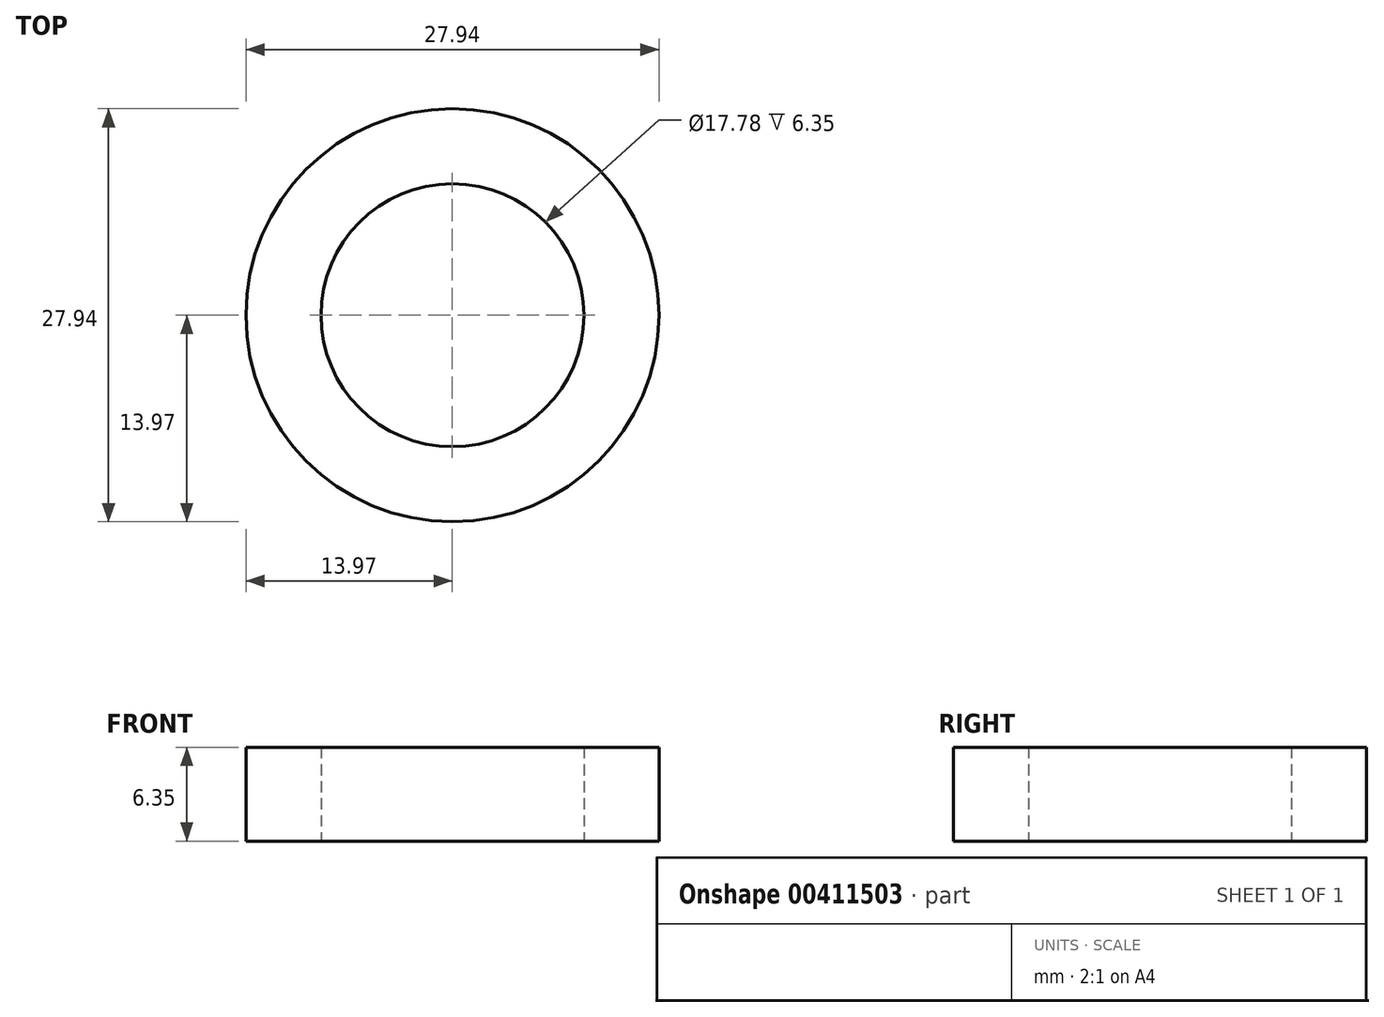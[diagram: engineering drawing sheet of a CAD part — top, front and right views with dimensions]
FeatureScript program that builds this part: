
annotation { "Feature Type Name" : "Feature", "Feature Type Description" : "" }
export const myFeature = defineFeature(function(context is Context, id is Id, definition is map)
    precondition{}
    {
        {
            var Q0;
            Q0=qCreatedBy(makeId("Top.planeOp"),FACE);
            var sketch = newSketch(context, id + "F0", { "sketchPlane" : qUnion([Q0])});
            skCircle(sketch, "E0", {"center": v(0, 0) * mm, "radius": 8.9 * mm});
            skCircle(sketch, "E1", {"center": v(0, 0) * mm, "radius": 13.97 * mm});
            skSolve(sketch);
        }
        {
            var Q0;
            Q0 = qSketchRegion(id + "F0", true);
            extrude(context, id + "F1", {"entities" : qUnion([Q0]), "depth" : 6.35 * mm});
        }
    });
